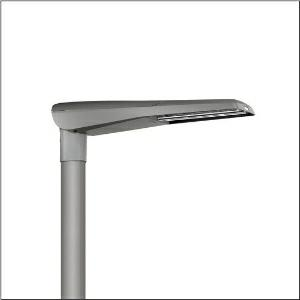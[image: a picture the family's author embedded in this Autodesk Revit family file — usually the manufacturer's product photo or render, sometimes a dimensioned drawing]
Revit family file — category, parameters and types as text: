
# Revit family: streetlight_sl_11_iq_mini___pc-r_5xc2fc1f08he_5d20
name_source: partatom
category: Lighting Fixtures
units: mm (PartAtom-declared; Revit-internal decimal feet)

## family parameters
Cut with Voids When Loaded = No
Host = Face
Light Source = No
Part Type = Normal
Room Calculation Point = No
Round Connector Dimension = Use Diameter
Shared = No

## types (1)
- --- (1 x LED, 5820 lm, 63.6 W, 2200K)
    Apparent Load = 64 VA
    CIE Flux Codes = 37 73 96 100 100
    Color Rendering = 70
    Color Temperature = 2200K
    Default Elevation = 1800 mm
    Description = Streetlight SL 11 iQ mini, mast luminaire, primary light control with 3 zone facetted reflector, of plastic, silver coated, highly specular, primary optical cover: cover, of PMMA, transparent, light distribution: PC-R, light emission: direct distribution, primary light characteristic: asymmetric, right, installation type: post-top, side-entry, lamps: LED, High Power LED, rated values: 7.110lm | 62,2W | 114,3lm/W (begin service life); end service life: 7.110lm | 65,6W; at 50% lumin. flux: 3.555lm | 29,4W | 120,9lm/W, colour temperature: 2200/2700/3000/4000K, colour rendering: CRI > 70, light colour: 722/727/730/740, light setting 1 begin service life: 100% | 7.110lm | 62,2W | 114,3lm/W | 3.000K, light setting 1 end service life: 65,6W, further light settings possible, control: Street-Remote, Auto-Match, Temp-Guard, Lumen-Switch, Night-Set, Smart-Wire, Light-Fading, Desk-Remote (wireless, voltage-free reading and setting of iQ features in the workshop via application-optimized NFC function/RFID function), optimised constant luminous flux control (CLO 2.0), with cable H07RN-F 3x 1.5mm², mains connection: 230..240V, AC, 50/60Hz, connection cable pre-assembled, cable length: 8,5m, luminaire housing, of diecast aluminium, powder-coated, SITECO metallic grey (DB 702S), please order mast flange separately, inclination adjustable without tools: 0°, 5°, 10°, 15° (post-top) | 0°, -5°, -10°, -15° (side-entry), sealing non-destructively replaceable, multi-level sealing system, length: 736mm, width: 174mm, height: 116mm, mast flange for spigot size: 42mm (side-entry): 5XC10008XM4, 60/48mm (side-entry/post-top): 5XC10108XM2, 76/60mm (side-entry/post-top): 5XC10108XM1, equipment: Power, protection rating (complete): IP66, insulation class (complete): insulation class II (safety insulation), certification: CE, ENEC, ENEC+, VDE, impact resistance: IK10, permissible operating ambient temperature for outdoor applications: -25..+50°C, standard-compliant lighting for roads and squares, Environmental Product Declaration (EPD) tested and certified by an independent institute, packaging unit: 1 piece

Light Distribution: PC-R
    Height = 116 mm
    Lamp = 1 x LED
    Lamp Light Flux = 5820 lm
    Lamp Power = 63.6 W
    Lamp count = 1
    Length = 736 mm
    Luminous efficacy = 92 lm/W
    Manufacturer = Siteco
    ModVariant = No
    Model = 5XC2FC1F08HE
    Number of Poles = 1
    OnlyDefault = Yes
    Power Factor = 1
    Product Name = Streetlight SL 11 iQ mini | PC-R
    Product group = mast luminaire | pylon top
    ProductGroupID = 6100
    Protection Class = Protection class II
    Protection Degree = IP 66
    RLX_Detail_Level = 1
    RLX_Emergency_Light_Flux = 0 lm
    RLX_Emergency_Type = 0
    RLX_Emergency_Type_DB = No
    RlxData = <blob elided: 57521 chars, md5=b1274080>
    Socket = socket
    Standby Power = 0 W
    System Light Flux = 5820 lm
    System Power = 64 W
    Type Comments = individual setting: luminous flux: 100 % | dim-lin: 254 | 866 mA
    Type Image = l_1003508.jpg
    URL = http://relux.com
    VarID = @adj_038783
    Voltage = 0 V
    Weight = 0.00 kg
    Width = 174 mm

## geometry (parser evidence)
native form markers: Blend x4, Sweep x13
no freeform markers — native parametric forms only
